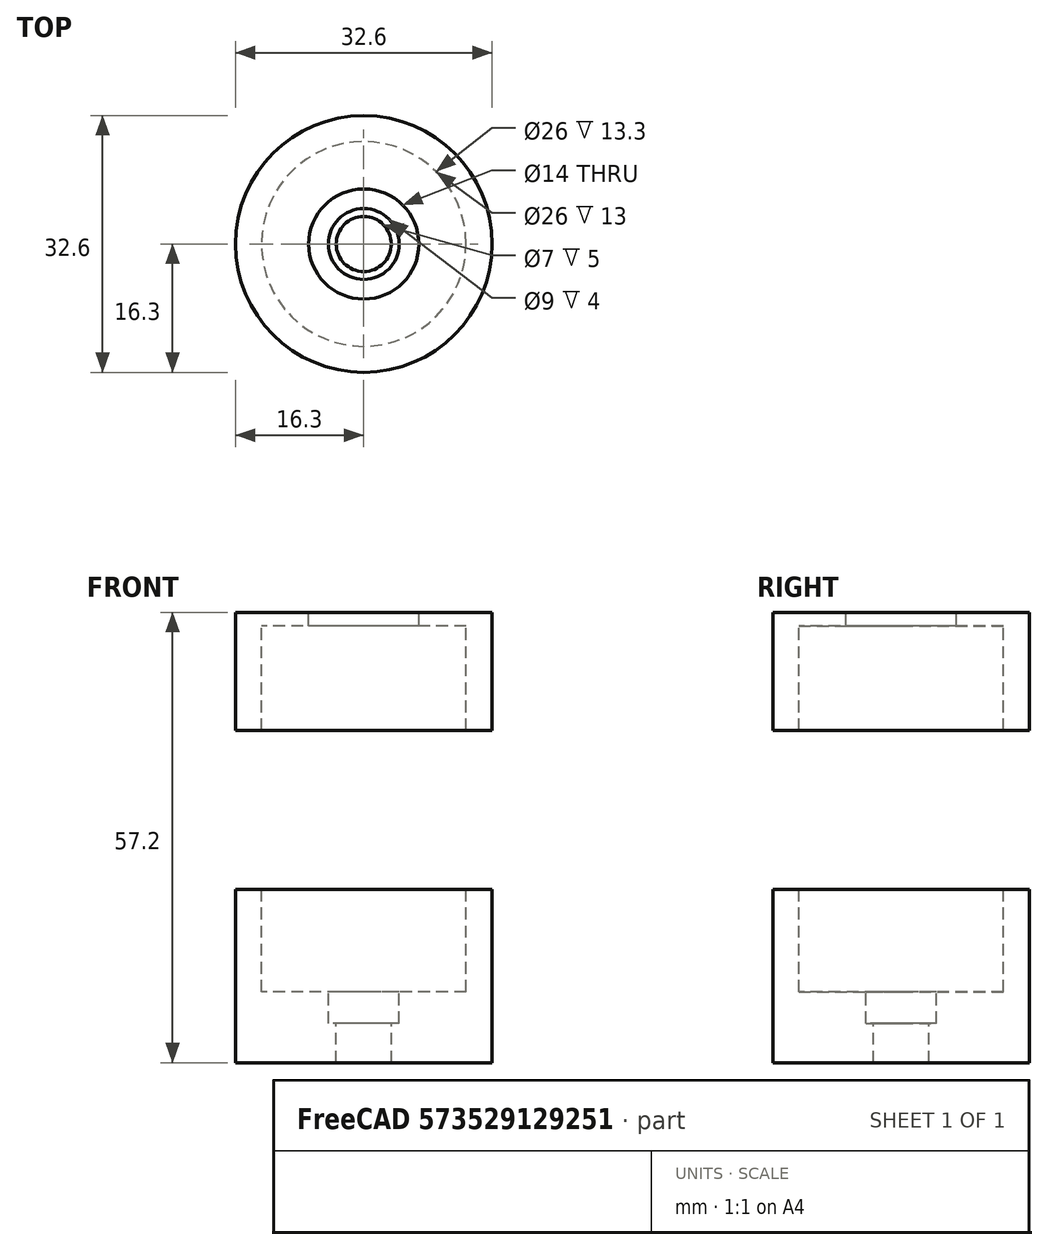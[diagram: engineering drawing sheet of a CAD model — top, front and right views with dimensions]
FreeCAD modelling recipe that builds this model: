
FCSTD DOCUMENT  (FreeCAD 0.15R4204 (Git))
Label: C_to_D_adapter
License: CC-BY 3.0
LicenseURL: http://creativecommons.org/licenses/by/3.0/
objects: Part::Cylinder×6, Part::Cut×2, Part::MultiFuse×1
note: 9 computed .brp shape members not serialized (recipe doc carries the construction recipe); baked Part::Feature solids carry a one-line shape summary decoded from their .brp

FEATURE [Part::Cylinder] Cylinder
  Angle = 360
  Height = 57.2
  Radius = 16.3
FEATURE [Part::Cylinder] Cylinder001
  Angle = 360
  Height = 46.5
  Placement = pos=(0,0,9) rot=(0,0,1;0rad)
  Radius = 13
FEATURE [Part::Cylinder] Cylinder002
  Angle = 360
  Height = 20
  Radius = 3.5
FEATURE [Part::Cylinder] Cylinder003
  Angle = 360
  Height = 20.2
  Placement = pos=(0,0,22) rot=(0,0,1;0rad)
  Radius = 20
FEATURE [Part::Cylinder] Cylinder004
  Angle = 360
  Height = 20
  Placement = pos=(0,0,38) rot=(0,0,1;0rad)
  Radius = 7
FEATURE [Part::Cylinder] Cylinder005
  Angle = 360
  Height = 20
  Placement = pos=(0,0,5) rot=(0,0,1;0rad)
  Radius = 4.5
FEATURE [Part::MultiFuse] Fusion
  Shapes = -> [Cylinder001,Cylinder004,Cylinder002,Cylinder005]
FEATURE [Part::Cut] Cut
  Base = -> Cylinder
  Tool = -> Fusion
FEATURE [Part::Cut] Cut001
  Base = -> Cut
  Tool = -> Cylinder003
